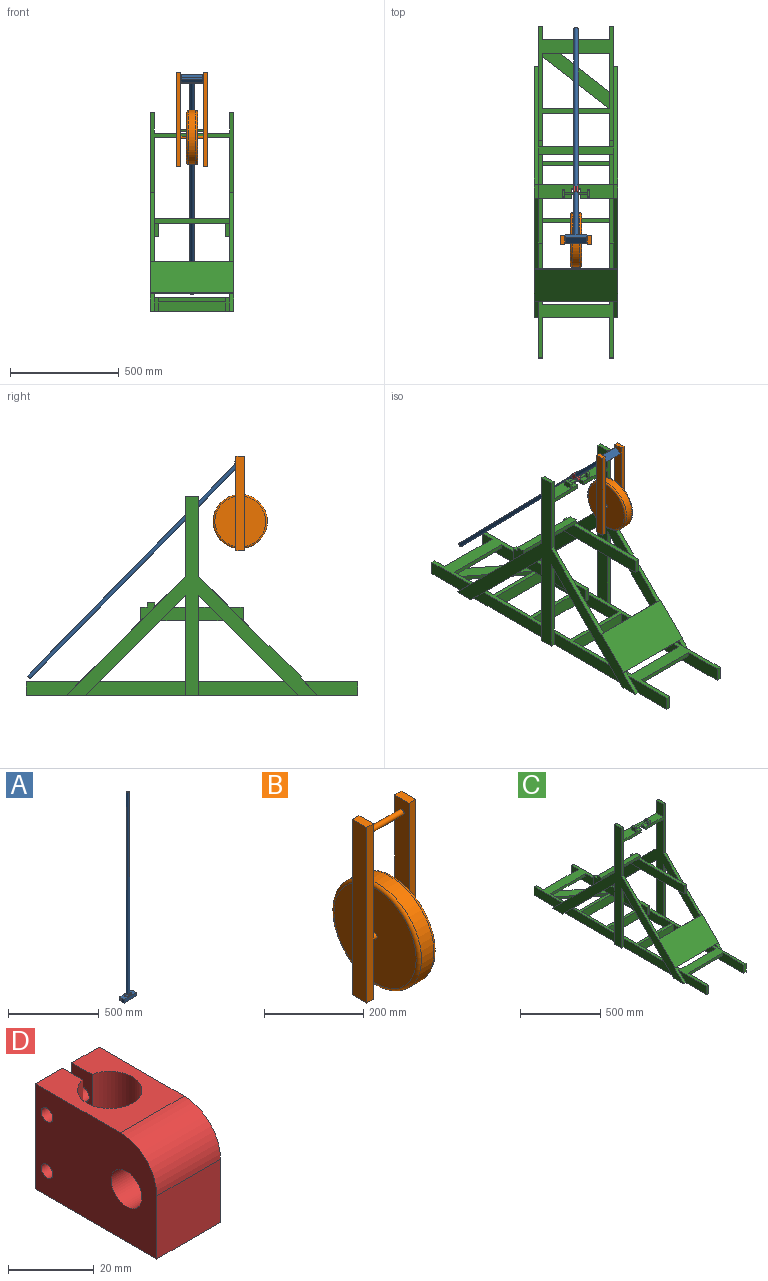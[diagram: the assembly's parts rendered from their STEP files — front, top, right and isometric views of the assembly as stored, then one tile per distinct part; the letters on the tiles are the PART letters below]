
ASSEMBLY  parts=4 mates=3
PART A: 28 faces, bbox 98.3x53.5x1390.8 mm
  f0: plane 42.18x36mm, normal (0,0,1), area 1155.4mm2, adj f4,f5,f6,f7,f8,f11,f16
  f1: cylinder r=7.5mm len=1371.6mm, axis (0,0,-1), area 64635.1mm2, adj f3,f26
  f2: cylinder r=9.25mm len=1358.6mm, axis (0,0,-1), area 78961.1mm2, adj f3,f15,f16,f17,f18
  f3: plane 18.5x18.5mm, normal (0,0,1), area 92.1mm2, adj f1,f2
  f4: plane 88.14x3.14mm, normal (0,1,0), area 264mm2, adj f0,f5,f13,f14,f15,f19
  f5: cylinder r=5mm len=5mm, axis (0,0,-1), area 23.6mm2, adj f0,f4,f6,f19
  f6: plane 36.07x22.05mm, normal (-1,0,0), area 638.5mm2, adj f0,f5,f7,f8,f19,f20,f22,f23
  f7: cylinder r=5mm len=5mm, axis (0,0,-1), area 23.6mm2, adj f0,f6,f8,f23
  f8: plane 98.26x22.19mm, normal (0,-1,0), area 2133.3mm2, adj f0,f6,f7,f9,f14,f18,f19,f20
  f9: cylinder r=5mm len=5mm, axis (0,0,-1), area 23.6mm2, adj f8,f10,f14,f19
  f10: plane 26x3mm, normal (1,0,0), area 78mm2, adj f9,f13,f14,f19
  f11: cylinder r=2.94mm len=5.88mm, axis (0,0,-1), area 55.5mm2, adj f0,f24
  f12: cylinder r=2.94mm len=5.88mm, axis (0,0,-1), area 55.5mm2, adj f14,f25
  f13: cylinder r=5mm len=5mm, axis (0,0,-1), area 23.6mm2, adj f4,f10,f14,f19
  f14: plane 42.18x36mm, normal (0,0,1), area 1155.4mm2, adj f4,f8,f9,f10,f12,f13,f17
  f15: bspline ~16.07x10.57mm, area 135.2mm2, adj f2,f4,f16,f17
  f16: torus R=19.25mm, axis (0,0,1), area 489.1mm2, adj f0,f2,f15,f18
  f17: torus R=19.25mm, axis (0,0,1), area 489.1mm2, adj f2,f14,f15,f18
  f18: bspline ~16.07x10.57mm, area 135.2mm2, adj f2,f8,f16,f17
  f19: plane 98.13x36.07mm, normal (0,0,1), area 27.8mm2, adj f4,f5,f6,f8,f9,f10,f13,f21
  f20: plane 98.13x36.07mm, normal (0,0,-1), area 3539.7mm2, adj f6,f8,f21,f22
  f21: plane 36.07x19.05mm, normal (1,0,0), area 560.5mm2, adj f8,f19,f20,f22,f27
  f22: plane 98.13x19.05mm, normal (0,1,0), area 1869.3mm2, adj f6,f19,f20,f21
  f23: plane 5x5mm, normal (0,0,1), area 5.4mm2, adj f6,f7,f8
  f24: plane 5.88x5.88mm, normal (0,0,1), area 27.2mm2, adj f11
  f25: plane 5.88x5.88mm, normal (0,0,1), area 27.2mm2, adj f12
  f26: plane 15x15mm, normal (0,0,1), area 176.7mm2, adj f1
  f27: cylinder r=6.35mm len=98.13mm, axis (-1,0,0), area 3915mm2, adj f6,f21
PART B: 20 faces, bbox 139.7x269.2x433 mm
  f0: cylinder r=6.35mm len=25.4mm, axis (-1,0,0), area 1013.4mm2, adj f4,f17
  f1: plane 40.64x19.05mm, normal (0,0,1), area 774.2mm2, adj f2,f4,f5,f6
  f2: plane 431.8x40.64mm, normal (-1,0,0), area 17548.4mm2, adj f1,f3,f5,f6
  f3: plane 40.64x19.05mm, normal (0,0,-1), area 774.2mm2, adj f2,f4,f5,f6
  f4: plane 431.8x40.64mm, normal (1,0,0), area 17295mm2, adj f0,f1,f3,f5,f6,f13
  f5: plane 431.8x19.05mm, normal (0,-1,0), area 8225.8mm2, adj f1,f2,f3,f4
  f6: plane 431.8x19.05mm, normal (0,1,0), area 8225.8mm2, adj f1,f2,f3,f4
  f7: plane 40.64x19.05mm, normal (0,0,1), area 774.2mm2, adj f8,f10,f11,f12
  f8: plane 431.8x40.64mm, normal (-1,0,0), area 17295mm2, adj f7,f9,f11,f12,f13,f14
  f9: plane 40.64x19.05mm, normal (0,0,-1), area 774.2mm2, adj f8,f10,f11,f12
  f10: plane 431.8x40.64mm, normal (1,0,0), area 17548.4mm2, adj f7,f9,f11,f12
  f11: plane 431.8x19.05mm, normal (0,-1,0), area 8225.8mm2, adj f7,f8,f9,f10
  f12: plane 431.8x19.05mm, normal (0,1,0), area 8225.8mm2, adj f7,f8,f9,f10
  f13: cylinder r=6.35mm len=101.6mm, axis (-1,0,0), area 4053.7mm2, adj f4,f8
  f14: cylinder r=6.35mm len=25.4mm, axis (-1,0,0), area 1013.4mm2, adj f8,f16
  f15: cylinder r=124.33mm len=248.67mm, axis (-1,0,0), area 27779.6mm2, adj f18,f19
  f16: plane 233.43x233.43mm, normal (1,0,0), area 42667.5mm2, adj f14,f19
  f17: plane 233.43x233.43mm, normal (-1,0,0), area 42667.5mm2, adj f0,f18
  f18: torus R=116.71mm, axis (1,0,0), area 9142.4mm2, adj f15,f17
  f19: torus R=116.71mm, axis (1,0,0), area 9142.4mm2, adj f15,f16
PART C: 123 faces, bbox 384.2x1524x914.4 mm
  f0: plane 28.69x19.05mm, normal (0,0,1), area 546.5mm2, adj f42,f43,f44,f105
  f1: plane 28.69x19.05mm, normal (0,0,1), area 546.5mm2, adj f86,f87,f88,f105
  f2: plane 393.7x342.15mm, normal (-1,0,0), area 41351.4mm2, adj f3,f24,f66,f67,f68,f69,f70,f72
  f3: plane 367.55x173.04mm, normal (0,-1,0), area 9935.3mm2, adj f2,f62,f71,f72,f73,f97,f98,f101
  f4: plane 95.25x62mm, normal (1,0,0), area 5905.6mm2, adj f24,f25,f26,f97
  f5: plane 81.46x81.46mm, normal (0,-0.71,0.71), area 2194.6mm2, adj f15,f20,f28,f31,f95
  f6: plane 81.46x81.46mm, normal (0,-0.71,0.71), area 2194.6mm2, adj f20,f63,f73,f76,f95
  f7: plane 307.98x63.5mm, normal (0,0,-1), area 16971.3mm2, adj f9,f56,f57,f90
  f8: plane 381x63.5mm, normal (1,0,0), area 21511.1mm2, adj f20,f32,f33,f54,f56,f57,f89,f90
  f9: plane 381x63.5mm, normal (-1,0,0), area 21511.1mm2, adj f7,f20,f33,f54,f56,f57,f77,f89
  f10: plane 222.25x63.5mm, normal (1,0,0), area 14112.9mm2, adj f20,f33,f52,f55
  f11: plane 241.3x63.5mm, normal (1,0,0), area 15322.6mm2, adj f20,f33,f51,f53
  f12: plane 222.25x63.5mm, normal (1,0,0), area 14112.9mm2, adj f20,f33,f49,f50
  f13: plane 381x63.5mm, normal (1,0,0), area 22983.8mm2, adj f20,f33,f34,f45,f46,f47,f48
  f14: plane 393.7x342.15mm, normal (1,0,0), area 41351.4mm2, adj f18,f19,f21,f22,f23,f24,f26,f27
  f15: plane 367.08x279.4mm, normal (1,0,0), area 24498.7mm2, adj f5,f18,f27,f33,f41,f93
  f16: plane 279.4x62mm, normal (1,0,0), area 17323.2mm2, adj f19,f21,f33,f41
  f17: plane 367.08x279.4mm, normal (1,0,0), area 24498.7mm2, adj f22,f23,f33,f41
  f18: plane 459.17x459.17mm, normal (0,0.71,-0.71), area 12370.3mm2, adj f14,f15,f19,f20,f28,f29,f37
  f19: plane 459.17x19.05mm, normal (0,-1,0), area 8747.1mm2, adj f14,f16,f18,f20,f28,f29,f37
  f20: plane 1524x384.18mm, normal (0,0,-1), area 90575.8mm2, adj f5,f6,f8,f9,f10,f11,f12,f13
  f21: plane 459.17x19.05mm, normal (0,1,0), area 8747.1mm2, adj f14,f16,f20,f22,f28,f30,f38
  f22: plane 459.17x459.17mm, normal (0,-0.71,-0.71), area 12370.3mm2, adj f14,f17,f20,f21,f28,f30,f38
  f23: plane 546.85x546.85mm, normal (0,0.71,0.71), area 14732.5mm2, adj f14,f17,f20,f24,f28,f35,f44
  f24: plane 384.18x367.55mm, normal (0,1,0), area 20596.4mm2, adj f2,f4,f14,f23,f25,f28,f62,f70
  f25: plane 62x19.05mm, normal (0,0,1), area 1181.1mm2, adj f4,f24,f26,f28
  f26: plane 367.55x173.04mm, normal (0,-1,0), area 9935.3mm2, adj f4,f14,f25,f27,f28,f97,f98,f100
  f27: plane 321.7x321.7mm, normal (0,-0.71,0.71), area 8667mm2, adj f14,f15,f26,f28,f36,f94
  f28: plane 1155.7x914.4mm, normal (-1,0,0), area 146195.1mm2, adj f5,f18,f19,f20,f21,f22,f23,f24
  f29: plane 459.17x63.5mm, normal (-1,0,0), area 27140.9mm2, adj f18,f19,f20,f33
  f30: plane 459.17x63.5mm, normal (-1,0,0), area 27140.9mm2, adj f20,f21,f22,f33
  f31: plane 247.65x63.5mm, normal (-1,0,0), area 13709.7mm2, adj f5,f20,f33,f34
  f32: plane 63.5x19.05mm, normal (0,1,0), area 1209.7mm2, adj f8,f20,f33,f35
  f33: plane 1524x346.08mm, normal (0,0,1), area 120644.9mm2, adj f8,f9,f10,f11,f12,f13,f15,f16
  f34: plane 63.5x19.05mm, normal (0,-1,0), area 1209.7mm2, adj f13,f20,f31,f33
  f35: plane 247.65x63.5mm, normal (-1,0,0), area 13709.6mm2, adj f20,f23,f32,f33
  f36: plane 63.5x63.5mm, normal (-1,0,0), area 2016.1mm2, adj f27,f39,f40
  f37: plane 116.27x63.5mm, normal (-1,0,0), area 5366.8mm2, adj f18,f19,f39,f41
  f38: plane 116.27x63.5mm, normal (-1,0,0), area 5366.8mm2, adj f21,f22,f39,f41
  f39: plane 405.65x19.05mm, normal (0,0,1), area 7727.6mm2, adj f14,f36,f37,f38,f40,f43,f106
  f40: plane 63.5x19.05mm, normal (0,-1,0), area 1209.7mm2, adj f36,f39,f41,f43
  f41: plane 469.9x19.05mm, normal (0,0,-1), area 8951.6mm2, adj f15,f16,f17,f37,f38,f40,f42,f43
  f42: plane 63.5x19.05mm, normal (0,1,0), area 1209.7mm2, adj f0,f41,f43,f44
  f43: plane 469.9x63.5mm, normal (1,0,0), area 29838.6mm2, adj f0,f39,f40,f41,f42,f104
  f44: plane 82.55x64.25mm, normal (-1,0,0), area 2693.3mm2, adj f0,f23,f42,f105,f106,f107
  f45: plane 307.98x19.05mm, normal (0,-1,0), area 5866.9mm2, adj f13,f33,f46,f61
  f46: plane 307.98x63.5mm, normal (0,0,-1), area 19556.4mm2, adj f13,f45,f47,f61
  f47: plane 307.98x19.05mm, normal (0,1,0), area 5866.9mm2, adj f13,f33,f46,f61
  f48: plane 307.98x63.5mm, normal (0,-1,0), area 19556.4mm2, adj f13,f20,f33,f61
  f49: plane 307.98x63.5mm, normal (0,1,0), area 19556.4mm2, adj f12,f20,f33,f60
  f50: plane 307.98x63.5mm, normal (0,-1,0), area 19556.4mm2, adj f12,f20,f33,f60
  f51: plane 307.98x63.5mm, normal (0,1,0), area 19556.4mm2, adj f11,f20,f33,f59
  f52: plane 307.98x63.5mm, normal (0,1,0), area 19556.4mm2, adj f10,f20,f33,f58
  f53: plane 307.98x63.5mm, normal (0,-1,0), area 19556.4mm2, adj f11,f20,f33,f59
  f54: plane 307.98x63.5mm, normal (0,1,0), area 19556.4mm2, adj f8,f9,f20,f33,f91
  f55: plane 307.98x63.5mm, normal (0,-1,0), area 19556.4mm2, adj f10,f20,f33,f58
  f56: plane 307.98x19.05mm, normal (0,-1,0), area 5866.9mm2, adj f7,f8,f9,f33,f89
  f57: plane 307.98x19.05mm, normal (0,1,0), area 5866.9mm2, adj f7,f8,f9,f33
  f58: plane 222.25x63.5mm, normal (-1,0,0), area 14112.9mm2, adj f20,f33,f52,f55
  f59: plane 241.3x63.5mm, normal (-1,0,0), area 15322.6mm2, adj f20,f33,f51,f53
  f60: plane 222.25x63.5mm, normal (-1,0,0), area 14112.9mm2, adj f20,f33,f49,f50
  f61: plane 381x63.5mm, normal (-1,0,0), area 22983.8mm2, adj f20,f33,f45,f46,f47,f48,f78
  f62: plane 95.25x62mm, normal (-1,0,0), area 5905.6mm2, adj f3,f24,f71,f97
  f63: plane 367.08x279.4mm, normal (-1,0,0), area 24498.7mm2, adj f6,f33,f66,f72,f85,f93
  f64: plane 279.4x62mm, normal (-1,0,0), area 17323.2mm2, adj f33,f67,f68,f85
  f65: plane 367.08x279.4mm, normal (-1,0,0), area 24498.7mm2, adj f33,f69,f70,f85
  f66: plane 459.17x459.17mm, normal (0,0.71,-0.71), area 12370.3mm2, adj f2,f20,f63,f67,f73,f74,f81
  f67: plane 459.17x19.05mm, normal (0,-1,0), area 8747.1mm2, adj f2,f20,f64,f66,f73,f74,f81
  f68: plane 459.17x19.05mm, normal (0,1,0), area 8747.1mm2, adj f2,f20,f64,f69,f73,f75,f82
  f69: plane 459.17x459.17mm, normal (0,-0.71,-0.71), area 12370.3mm2, adj f2,f20,f65,f68,f73,f75,f82
  f70: plane 546.85x546.85mm, normal (0,0.71,0.71), area 14732.5mm2, adj f2,f20,f24,f65,f73,f79,f88
  f71: plane 62x19.05mm, normal (0,0,1), area 1181.1mm2, adj f3,f24,f62,f73
  f72: plane 321.7x321.7mm, normal (0,-0.71,0.71), area 8667mm2, adj f2,f3,f63,f73,f80,f94
  f73: plane 1155.7x914.4mm, normal (1,0,0), area 146195.1mm2, adj f3,f6,f20,f24,f66,f67,f68,f69
  f74: plane 459.17x63.5mm, normal (1,0,0), area 27140.9mm2, adj f20,f33,f66,f67
  f75: plane 459.17x63.5mm, normal (1,0,0), area 27140.9mm2, adj f20,f33,f68,f69
  f76: plane 247.65x63.5mm, normal (1,0,0), area 13709.7mm2, adj f6,f20,f33,f78
  f77: plane 63.5x19.05mm, normal (0,1,0), area 1209.7mm2, adj f9,f20,f33,f79
  f78: plane 63.5x19.05mm, normal (0,-1,0), area 1209.7mm2, adj f20,f33,f61,f76
  f79: plane 247.65x63.5mm, normal (1,0,0), area 13709.6mm2, adj f20,f33,f70,f77
  f80: plane 63.5x63.5mm, normal (1,0,0), area 2016.1mm2, adj f72,f83,f84
  f81: plane 116.27x63.5mm, normal (1,0,0), area 5366.8mm2, adj f66,f67,f83,f85
  f82: plane 116.27x63.5mm, normal (1,0,0), area 5366.8mm2, adj f68,f69,f83,f85
  f83: plane 405.65x19.05mm, normal (0,0,1), area 7727.6mm2, adj f2,f80,f81,f82,f84,f87,f106
  f84: plane 63.5x19.05mm, normal (0,-1,0), area 1209.7mm2, adj f80,f83,f85,f87
  f85: plane 469.9x19.05mm, normal (0,0,-1), area 8951.6mm2, adj f63,f64,f65,f81,f82,f84,f86,f87
  f86: plane 63.5x19.05mm, normal (0,1,0), area 1209.7mm2, adj f1,f85,f87,f88
  f87: plane 469.9x63.5mm, normal (-1,0,0), area 29838.6mm2, adj f1,f83,f84,f85,f86,f104
  f88: plane 82.55x64.25mm, normal (1,0,0), area 2693.3mm2, adj f1,f70,f86,f105,f106,f107
  f89: plane 307.98x254mm, normal (0,0,1), area 21223.8mm2, adj f8,f9,f56,f90,f91
  f90: plane 307.98x240.19mm, normal (0.61,0.79,0), area 7440.3mm2, adj f7,f8,f9,f89,f92
  f91: plane 307.98x240.19mm, normal (-0.61,-0.79,0), area 7440.3mm2, adj f8,f54,f89,f92
  f92: plane 317.5x307.98mm, normal (0,0,-1), area 23808.8mm2, adj f8,f9,f90,f91
  f93: plane 346.08x143.68mm, normal (0,0.71,-0.71), area 70322.4mm2, adj f15,f63,f94,f95
  f94: plane 384.18x4.49mm, normal (0,0.71,0.71), area 2439.5mm2, adj f27,f28,f72,f73,f93,f96
  f95: plane 384.18x4.49mm, normal (0,-0.71,-0.71), area 2439.5mm2, adj f5,f6,f28,f73,f93,f96
  f96: plane 384.18x143.68mm, normal (0,-0.71,0.71), area 78064.4mm2, adj f28,f73,f94,f95
  f97: plane 346.08x62mm, normal (0,0,1), area 18699.1mm2, adj f3,f4,f24,f26,f62,f100,f101,f103
  f98: plane 346.08x62mm, normal (0,0,-1), area 19666.8mm2, adj f2,f3,f14,f24,f26,f100,f101,f102
  f99: plane 38.1x6.35mm, normal (0,-1,0), area 241.9mm2, adj f100,f101,f102,f103
  f100: plane 46.99x19.05mm, normal (1,0,0), area 791.5mm2, adj f26,f97,f98,f99,f102,f103
  f101: plane 46.99x19.05mm, normal (-1,0,0), area 791.5mm2, adj f3,f97,f98,f99,f102,f103
  f102: cylinder r=6.35mm len=38.1mm, axis (-1,0,0), area 380mm2, adj f98,f99,f100,f101
  f103: cylinder r=6.35mm len=38.1mm, axis (1,0,0), area 380mm2, adj f97,f99,f100,f101
  f104: plane 307.98x35.56mm, normal (0,0,-1), area 10951.6mm2, adj f43,f87,f105,f106
  f105: plane 346.08x19.05mm, normal (0,1,0), area 6592.7mm2, adj f0,f1,f44,f88,f104,f107
  f106: plane 346.08x19.05mm, normal (0,-1,0), area 6592.7mm2, adj f2,f14,f39,f44,f83,f88,f104,f107
  f107: plane 346.08x35.56mm, normal (0,0,1), area 12306.4mm2, adj f44,f88,f105,f106
  f108: plane 20.32x12.7mm, normal (0,1,0), area 258.1mm2, adj f97,f109,f111,f118
  f109: plane 38.1x25.4mm, normal (-1,0,0), area 956.7mm2, adj f97,f108,f110,f112,f118,f119
  f110: plane 20.32x12.7mm, normal (0,-1,0), area 258.1mm2, adj f97,f109,f111,f119
  f111: plane 38.1x25.4mm, normal (1,0,0), area 878.1mm2, adj f97,f108,f110,f112,f118,f119,f122
  f112: plane 27.94x12.7mm, normal (0,0,1), area 354.8mm2, adj f109,f111,f118,f119
  f113: plane 38.1x25.4mm, normal (1,0,0), area 956.7mm2, adj f97,f114,f116,f117,f120,f121
  f114: plane 20.32x12.7mm, normal (0,1,0), area 258.1mm2, adj f97,f113,f115,f120
  f115: plane 38.1x25.4mm, normal (-1,0,0), area 878.1mm2, adj f97,f114,f116,f117,f120,f121,f122
  f116: plane 20.32x12.7mm, normal (0,-1,0), area 258.1mm2, adj f97,f113,f115,f121
  f117: plane 27.94x12.7mm, normal (0,0,1), area 354.8mm2, adj f113,f115,f120,f121
  f118: cylinder r=5.08mm len=12.7mm, axis (1,0,0), area 101.3mm2, adj f108,f109,f111,f112
  f119: cylinder r=5.08mm len=12.7mm, axis (-1,0,0), area 101.3mm2, adj f109,f110,f111,f112
  f120: cylinder r=5.08mm len=12.7mm, axis (1,0,0), area 101.3mm2, adj f113,f114,f115,f117
  f121: cylinder r=5.08mm len=12.7mm, axis (-1,0,0), area 101.3mm2, adj f113,f115,f116,f117
  f122: cylinder r=5mm len=101.6mm, axis (1,0,0), area 3191.9mm2, adj f111,f115
PART D: 16 faces, bbox 21x40x30 mm
  f0: plane 30x9mm, normal (0,1,0), area 270mm2, adj f1,f7,f8,f9
  f1: plane 30x6.65mm, normal (-1,0,0), area 176.9mm2, adj f0,f2,f8,f9,f11,f12
  f2: cylinder r=7.5mm len=30mm, axis (0,0,-1), area 1323.1mm2, adj f1,f3,f8,f9
  f3: plane 30x6.65mm, normal (1,0,0), area 176.9mm2, adj f2,f4,f8,f9,f14,f15
  f4: plane 30x9mm, normal (0,1,0), area 270mm2, adj f3,f5,f8,f9
  f5: plane 40x30mm, normal (-1,0,0), area 1066.3mm2, adj f4,f6,f8,f9,f10,f13,f14,f15
  f6: plane 21x18mm, normal (0,-1,0), area 378mm2, adj f5,f7,f9,f10
  f7: plane 40x30mm, normal (1,0,0), area 1066.3mm2, adj f0,f6,f8,f9,f10,f11,f12,f13
  f8: plane 28x21mm, normal (0,0,1), area 391.6mm2, adj f0,f1,f2,f3,f4,f5,f7,f10
  f9: plane 40x21mm, normal (0,0,-1), area 643.6mm2, adj f0,f1,f2,f3,f4,f5,f6,f7
  f10: cylinder r=12mm len=21mm, axis (-1,0,0), area 395.8mm2, adj f5,f6,f7,f8
  f11: cylinder r=1.9mm len=9mm, axis (-1,0,0), area 107.4mm2, adj f1,f7
  f12: cylinder r=1.9mm len=9mm, axis (-1,0,0), area 107.4mm2, adj f1,f7
  f13: cylinder r=5.05mm len=21mm, axis (-1,0,0), area 666.3mm2, adj f5,f7
  f14: cylinder r=1.9mm len=9mm, axis (-1,0,0), area 107.4mm2, adj f3,f5
  f15: cylinder r=1.9mm len=9mm, axis (-1,0,0), area 107.4mm2, adj f3,f5
PLACE A rot(axis=(-1,0,0),135.6deg) t=(-47.91,-349.71,767.95)mm
PLACE B t=(-47.84,-360.21,586.84)mm
PLACE C t=(-239.99,-138.63,-294.99)mm
PLACE D rot(axis=(1,0,0),44.4deg) t=(-58.41,-114.21,547.64)mm
MATE slider A.f2 <-> D.f2  axis (0,-0.7,0.71) through (-47.91,131.96,276.43)mm
MATE revolute D.f13 <-> C.f122  axis (-1,0,0) through (-47.91,-146.14,537.35)mm
MATE revolute B.f13 <-> A.f27  axis (-1,0,0) through (-47.84,-360.21,770.99)mm
